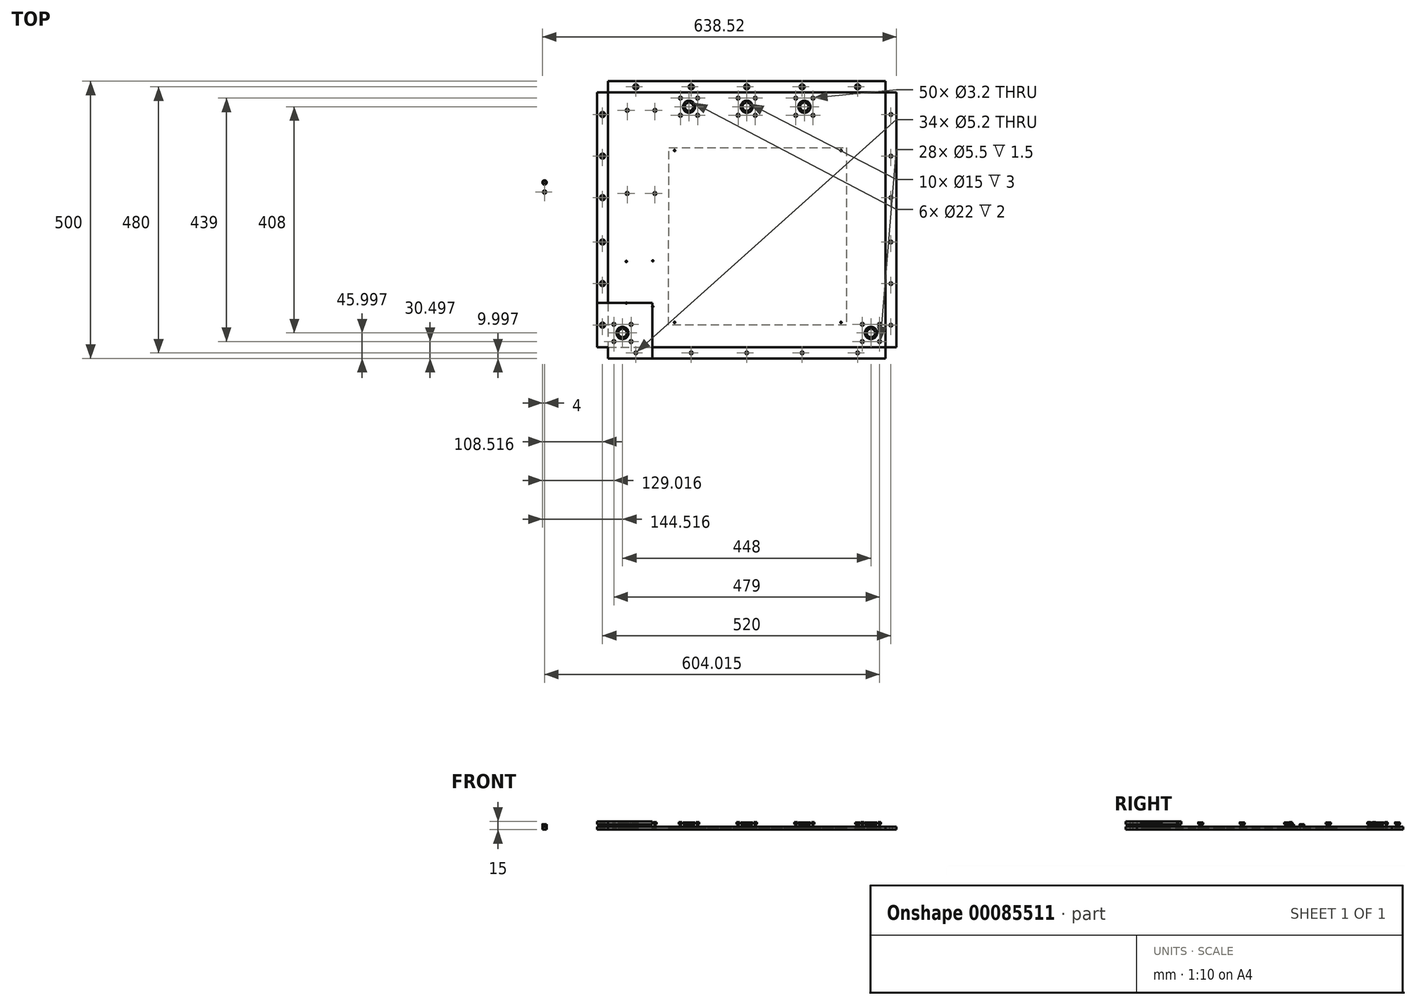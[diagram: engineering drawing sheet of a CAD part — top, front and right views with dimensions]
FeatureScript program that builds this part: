
annotation { "Feature Type Name" : "Feature", "Feature Type Description" : "" }
export const myFeature = defineFeature(function(context is Context, id is Id, definition is map)
    precondition{}
    {
        {
            var Q0;
            Q0=qCreatedBy(makeId("Top.planeOp"),FACE);
            var sketch = newSketch(context, id + "F0", { "sketchPlane" : qUnion([Q0])});
            skLineSegment(sketch, "E0.bottom", {"start": v(-237.36, 309.29) * mm, "end": v(262.64, 309.29) * mm, "construction": true});
            skLineSegment(sketch, "E0.top", {"start": v(-237.36, -150.71) * mm, "end": v(262.64, -150.71) * mm, "construction": true});
            skLineSegment(sketch, "E0.left", {"start": v(-237.36, 309.29) * mm, "end": v(-237.36, -150.71) * mm, "construction": true});
            skLineSegment(sketch, "E0.right", {"start": v(262.64, 309.29) * mm, "end": v(262.64, -150.71) * mm, "construction": true});
            skLineSegment(sketch, "E1.0", {"start": v(-118.36, 309.29) * mm, "end": v(-118.36, -150.71) * mm, "construction": true});
            skLineSegment(sketch, "E2.0", {"start": v(-237.36, 94.29) * mm, "end": v(-117.36, 94.29) * mm, "construction": true});
            skLineSegment(sketch, "E3.0", {"start": v(-202.86, 309.29) * mm, "end": v(-202.86, 94.29) * mm, "construction": true});
            skLineSegment(sketch, "E4.0", {"start": v(-152.86, 309.29) * mm, "end": v(-152.86, 94.29) * mm, "construction": true});
            skLineSegment(sketch, "E5.0", {"start": v(-201.3, 276.79) * mm, "end": v(-118.36, 276.79) * mm, "construction": true});
            skLineSegment(sketch, "E6.0", {"start": v(-201.3, 126.79) * mm, "end": v(-118.36, 126.79) * mm, "construction": true});
            skCircle(sketch, "E7", {"center": v(-202.86, 276.79) * mm, "radius": 1.6 * mm});
            skCircle(sketch, "E8", {"center": v(-152.86, 276.79) * mm, "radius": 1.6 * mm});
            skCircle(sketch, "E9", {"center": v(-152.86, 126.79) * mm, "radius": 1.6 * mm});
            skCircle(sketch, "E10", {"center": v(-202.86, 126.79) * mm, "radius": 1.6 * mm});
            skLineSegment(sketch, "E11.0", {"start": v(182.64, 309.29) * mm, "end": v(182.64, -150.71) * mm, "construction": true});
            skLineSegment(sketch, "E12.0", {"start": v(-117.36, 309.29) * mm, "end": v(-117.36, -150.71) * mm, "construction": true});
            skLineSegment(sketch, "E13.0", {"start": v(197.64, 309.29) * mm, "end": v(197.64, -150.71) * mm, "construction": true});
            skLineSegment(sketch, "E14.0", {"start": v(-132.36, 309.29) * mm, "end": v(-132.36, -150.71) * mm, "construction": true});
            skLineSegment(sketch, "E15.0", {"start": v(-237.36, -140.21) * mm, "end": v(262.64, -140.21) * mm, "construction": true});
            skLineSegment(sketch, "E16.0", {"start": v(-237.36, 298.79) * mm, "end": v(262.64, 298.79) * mm, "construction": true});
            skLineSegment(sketch, "E17.0", {"start": v(-237.36, -109.21) * mm, "end": v(262.64, -109.21) * mm, "construction": true});
            skLineSegment(sketch, "E18.trimOffspring", {"start": v(-226.86, -109.21) * mm, "end": v(-226.86, -140.21) * mm, "construction": true});
            skLineSegment(sketch, "E19.trimOffspring", {"start": v(-195.86, -109.21) * mm, "end": v(-195.86, -140.21) * mm, "construction": true});
            skLineSegment(sketch, "E20", {"start": v(-226.86, -124.71) * mm, "end": v(-195.86, -124.71) * mm, "construction": true});
            skCircle(sketch, "E21", {"center": v(-226.86, -109.21) * mm, "radius": 1.6 * mm});
            skCircle(sketch, "E22", {"center": v(-195.86, -109.21) * mm, "radius": 1.6 * mm});
            skCircle(sketch, "E23", {"center": v(-195.86, -140.21) * mm, "radius": 1.6 * mm});
            skCircle(sketch, "E24", {"center": v(-226.86, -140.21) * mm, "radius": 1.6 * mm});
            skLineSegment(sketch, "E25.trimOffspring", {"start": v(252.14, -109.21) * mm, "end": v(252.14, -140.21) * mm, "construction": true});
            skLineSegment(sketch, "E26.trimOffspring", {"start": v(221.14, -109.21) * mm, "end": v(221.14, -140.21) * mm, "construction": true});
            skLineSegment(sketch, "E27", {"start": v(221.14, -124.71) * mm, "end": v(252.14, -124.71) * mm, "construction": true});
            skCircle(sketch, "E28", {"center": v(221.14, -109.21) * mm, "radius": 1.6 * mm});
            skCircle(sketch, "E29", {"center": v(252.14, -109.21) * mm, "radius": 1.6 * mm});
            skCircle(sketch, "E30", {"center": v(221.14, -140.21) * mm, "radius": 1.6 * mm});
            skCircle(sketch, "E31", {"center": v(252.14, -140.21) * mm, "radius": 1.6 * mm});
            skLineSegment(sketch, "E32.0", {"start": v(-106.86, 309.29) * mm, "end": v(-106.86, 199.29) * mm, "construction": true});
            skLineSegment(sketch, "E33.trimOffspring", {"start": v(197.64, -100.71) * mm, "end": v(262.64, -100.71) * mm, "construction": true});
            skLineSegment(sketch, "E34.trimOffspring", {"start": v(-118.36, 199.29) * mm, "end": v(182.64, 199.29) * mm, "construction": true});
            skLineSegment(sketch, "E35.trimOffspring", {"start": v(-118.36, -100.71) * mm, "end": v(182.64, -100.71) * mm, "construction": true});
            skLineSegment(sketch, "E36.0", {"start": v(132.14, 199.29) * mm, "end": v(132.14, 309.29) * mm, "construction": true});
            skLineSegment(sketch, "E37.0", {"start": v(-75.86, 298.79) * mm, "end": v(-75.86, 267.79) * mm, "construction": true});
            skLineSegment(sketch, "E38.0", {"start": v(101.14, 267.79) * mm, "end": v(101.14, 298.79) * mm, "construction": true});
            skLineSegment(sketch, "E39.0", {"start": v(-237.36, 267.79) * mm, "end": v(262.64, 267.79) * mm, "construction": true});
            skLineSegment(sketch, "E40", {"start": v(101.14, 283.29) * mm, "end": v(132.14, 283.29) * mm, "construction": true});
            skLineSegment(sketch, "E41", {"start": v(-75.86, 283.29) * mm, "end": v(-106.86, 283.29) * mm, "construction": true});
            skCircle(sketch, "E42", {"center": v(101.14, 298.79) * mm, "radius": 1.6 * mm});
            skCircle(sketch, "E43", {"center": v(101.14, 267.79) * mm, "radius": 1.6 * mm});
            skCircle(sketch, "E44", {"center": v(132.14, 298.79) * mm, "radius": 1.6 * mm});
            skCircle(sketch, "E45", {"center": v(132.14, 267.79) * mm, "radius": 1.6 * mm});
            skCircle(sketch, "E46", {"center": v(-75.86, 267.79) * mm, "radius": 1.6 * mm});
            skCircle(sketch, "E47", {"center": v(-75.86, 298.79) * mm, "radius": 1.6 * mm});
            skCircle(sketch, "E48", {"center": v(-106.86, 298.79) * mm, "radius": 1.6 * mm});
            skCircle(sketch, "E49", {"center": v(-106.86, 267.79) * mm, "radius": 1.6 * mm});
            skCircle(sketch, "E50", {"center": v(116.64, 283.29) * mm, "radius": 7.5 * mm});
            skCircle(sketch, "E51", {"center": v(-91.36, 283.29) * mm, "radius": 7.5 * mm});
            skLineSegment(sketch, "E52.0", {"start": v(-237.36, 329.29) * mm, "end": v(262.64, 329.29) * mm});
            skLineSegment(sketch, "E53.0", {"start": v(282.64, 309.29) * mm, "end": v(282.64, -150.71) * mm});
            skLineSegment(sketch, "E54.0", {"start": v(-257.36, 309.29) * mm, "end": v(-257.36, -150.71) * mm});
            skLineSegment(sketch, "E55.0", {"start": v(-237.36, -170.71) * mm, "end": v(262.64, -170.71) * mm});
            skLineSegment(sketch, "E56.0", {"start": v(-237.36, 19.29) * mm, "end": v(-117.36, 19.29) * mm, "construction": true});
            skLineSegment(sketch, "E57.0", {"start": v(-237.36, -84.57) * mm, "end": v(-117.36, -84.57) * mm, "construction": true});
            skLineSegment(sketch, "E58.trimOffspring", {"start": v(-207.36, 19.29) * mm, "end": v(-207.36, -84.57) * mm, "construction": true});
            skLineSegment(sketch, "E59.trimOffspring", {"start": v(-204.36, 19.29) * mm, "end": v(-204.36, -84.57) * mm, "construction": true});
            skLineSegment(sketch, "E60.trimOffspring", {"start": v(-156.66, 19.29) * mm, "end": v(-156.66, -84.57) * mm, "construction": true});
            skLineSegment(sketch, "E61.trimOffspring", {"start": v(-146.14, 19.29) * mm, "end": v(-146.14, -84.57) * mm, "construction": true});
            skLineSegment(sketch, "E62.0", {"start": v(-207.36, 5.39) * mm, "end": v(-146.14, 5.39) * mm, "construction": true});
            skLineSegment(sketch, "E63.0", {"start": v(-207.36, 4.14) * mm, "end": v(-146.14, 4.14) * mm, "construction": true});
            skLineSegment(sketch, "E64.0", {"start": v(-207.36, -70.81) * mm, "end": v(-146.14, -70.81) * mm, "construction": true});
            skLineSegment(sketch, "E65.0", {"start": v(-207.36, -77.16) * mm, "end": v(-146.14, -77.16) * mm, "construction": true});
            skCircle(sketch, "E66", {"center": v(-204.36, 4.14) * mm, "radius": 1.25 * mm});
            skCircle(sketch, "E67", {"center": v(-156.66, 5.39) * mm, "radius": 1.25 * mm});
            skCircle(sketch, "E68", {"center": v(-156.66, -77.16) * mm, "radius": 1.25 * mm});
            skCircle(sketch, "E69", {"center": v(-204.36, -70.81) * mm, "radius": 1.25 * mm});
            skLineSegment(sketch, "E70", {"start": v(262.64, 329.29) * mm, "end": v(262.64, 309.29) * mm});
            skLineSegment(sketch, "E71", {"start": v(262.64, 309.29) * mm, "end": v(282.64, 309.29) * mm});
            skLineSegment(sketch, "E72", {"start": v(-237.36, 329.29) * mm, "end": v(-237.36, 309.29) * mm});
            skLineSegment(sketch, "E73", {"start": v(-257.36, 309.29) * mm, "end": v(-237.36, 309.29) * mm});
            skLineSegment(sketch, "E74", {"start": v(-257.36, -150.71) * mm, "end": v(-237.36, -150.71) * mm});
            skLineSegment(sketch, "E75", {"start": v(-237.36, -170.71) * mm, "end": v(-237.36, -150.71) * mm});
            skLineSegment(sketch, "E76", {"start": v(262.64, -170.71) * mm, "end": v(262.64, -150.71) * mm});
            skLineSegment(sketch, "E77", {"start": v(282.64, -150.71) * mm, "end": v(262.64, -150.71) * mm});
            skLineSegment(sketch, "E78.0", {"start": v(-237.36, 319.29) * mm, "end": v(262.64, 319.29) * mm, "construction": true});
            skLineSegment(sketch, "E79.0", {"start": v(-247.36, 309.29) * mm, "end": v(-247.36, -150.71) * mm, "construction": true});
            skLineSegment(sketch, "E80.0", {"start": v(-257.36, -110.71) * mm, "end": v(-237.36, -110.71) * mm, "construction": true});
            skLineSegment(sketch, "E81.0", {"start": v(-257.36, -35.71) * mm, "end": v(-237.36, -35.71) * mm, "construction": true});
            skLineSegment(sketch, "E82.0", {"start": v(-257.36, 39.29) * mm, "end": v(-237.36, 39.29) * mm, "construction": true});
            skLineSegment(sketch, "E83.0", {"start": v(-257.36, 119.29) * mm, "end": v(-237.36, 119.29) * mm, "construction": true});
            skLineSegment(sketch, "E84.0", {"start": v(-257.36, 194.29) * mm, "end": v(-237.36, 194.29) * mm, "construction": true});
            skLineSegment(sketch, "E85.0", {"start": v(-257.36, 269.29) * mm, "end": v(-237.36, 269.29) * mm, "construction": true});
            skCircle(sketch, "E86", {"center": v(-247.36, 39.29) * mm, "radius": 2.6 * mm});
            skCircle(sketch, "E87", {"center": v(-247.36, 119.29) * mm, "radius": 2.6 * mm});
            skCircle(sketch, "E88", {"center": v(-247.36, 194.29) * mm, "radius": 2.6 * mm});
            skCircle(sketch, "E89", {"center": v(-247.36, 269.29) * mm, "radius": 2.6 * mm});
            skCircle(sketch, "E90", {"center": v(-247.36, -35.71) * mm, "radius": 2.6 * mm});
            skCircle(sketch, "E91", {"center": v(-247.36, -110.71) * mm, "radius": 2.6 * mm});
            skLineSegment(sketch, "E92", {"start": v(12.64, 329.29) * mm, "end": v(12.64, 425.64) * mm});
            skCircle(sketch, "E93.MirrorC", {"center": v(272.64, -110.71) * mm, "radius": 2.6 * mm});
            skCircle(sketch, "E94.MirrorC", {"center": v(272.64, -35.71) * mm, "radius": 2.6 * mm});
            skCircle(sketch, "E95.MirrorC", {"center": v(272.64, 39.29) * mm, "radius": 2.6 * mm});
            skCircle(sketch, "E96.MirrorC", {"center": v(272.64, 119.29) * mm, "radius": 2.6 * mm});
            skCircle(sketch, "E97.MirrorC", {"center": v(272.64, 194.29) * mm, "radius": 2.6 * mm});
            skCircle(sketch, "E98.MirrorC", {"center": v(272.64, 269.29) * mm, "radius": 2.6 * mm});
            skLineSegment(sketch, "E99.0", {"start": v(-187.36, 329.29) * mm, "end": v(-187.36, 309.29) * mm, "construction": true});
            skLineSegment(sketch, "E100.0", {"start": v(-87.36, 329.29) * mm, "end": v(-87.36, 309.29) * mm, "construction": true});
            skLineSegment(sketch, "E101.0", {"start": v(212.64, 329.29) * mm, "end": v(212.64, 309.29) * mm, "construction": true});
            skLineSegment(sketch, "E102.0", {"start": v(112.64, 329.29) * mm, "end": v(112.64, 309.29) * mm, "construction": true});
            skCircle(sketch, "E103", {"center": v(-187.36, 319.29) * mm, "radius": 2.6 * mm});
            skCircle(sketch, "E104", {"center": v(-87.36, 319.29) * mm, "radius": 2.6 * mm});
            skCircle(sketch, "E105", {"center": v(12.64, 319.29) * mm, "radius": 2.6 * mm});
            skCircle(sketch, "E106", {"center": v(112.64, 319.29) * mm, "radius": 2.6 * mm});
            skCircle(sketch, "E107", {"center": v(212.64, 319.29) * mm, "radius": 2.6 * mm});
            skLineSegment(sketch, "E108", {"start": v(282.64, 79.29) * mm, "end": v(335.67, 79.29) * mm});
            skCircle(sketch, "E109.MirrorC", {"center": v(212.64, -160.71) * mm, "radius": 2.6 * mm});
            skCircle(sketch, "E110.MirrorC", {"center": v(112.64, -160.71) * mm, "radius": 2.6 * mm});
            skCircle(sketch, "E111.MirrorC", {"center": v(12.64, -160.71) * mm, "radius": 2.6 * mm});
            skCircle(sketch, "E112.MirrorC", {"center": v(-87.36, -160.71) * mm, "radius": 2.6 * mm});
            skCircle(sketch, "E113.MirrorC", {"center": v(-187.36, -160.71) * mm, "radius": 2.6 * mm});
            skCircle(sketch, "E114", {"center": v(-211.36, -124.71) * mm, "radius": 7.5 * mm});
            skCircle(sketch, "E115", {"center": v(236.64, -124.71) * mm, "radius": 7.5 * mm});
            skLineSegment(sketch, "E116", {"start": v(12.64, 267.79) * mm, "end": v(12.64, 298.79) * mm, "construction": true});
            skLineSegment(sketch, "E117.0", {"start": v(28.14, 267.79) * mm, "end": v(28.14, 298.79) * mm, "construction": true});
            skLineSegment(sketch, "E118.0", {"start": v(-2.86, 267.79) * mm, "end": v(-2.86, 298.79) * mm, "construction": true});
            skCircle(sketch, "E119", {"center": v(12.64, 283.29) * mm, "radius": 7.5 * mm});
            skCircle(sketch, "E120", {"center": v(-2.86, 298.79) * mm, "radius": 1.6 * mm});
            skCircle(sketch, "E121", {"center": v(28.14, 298.79) * mm, "radius": 1.6 * mm});
            skCircle(sketch, "E122", {"center": v(28.14, 267.79) * mm, "radius": 1.6 * mm});
            skCircle(sketch, "E123", {"center": v(-2.86, 267.79) * mm, "radius": 1.6 * mm});
            skSolve(sketch);
        }
        {
            var Q0;
            Q0=qCreatedBy(makeId("Top.planeOp"),FACE);
            var sketch = newSketch(context, id + "F1", { "sketchPlane" : qUnion([Q0])});
            skLineSegment(sketch, "E124.bottom", {"start": v(-558.04, 48.55) * mm, "end": v(-516.04, 48.55) * mm, "construction": true});
            skLineSegment(sketch, "E124.top", {"start": v(-558.04, 1.55) * mm, "end": v(-516.04, 1.55) * mm, "construction": true});
            skLineSegment(sketch, "E124.right", {"start": v(-516.04, 48.55) * mm, "end": v(-516.04, 1.55) * mm, "construction": true});
            skLineSegment(sketch, "E125", {"start": v(-558.04, -28.45) * mm, "end": v(-558.04, 1.55) * mm});
            skLineSegment(sketch, "E126.1", {"start": v(-515.04, 48.55) * mm, "end": v(-515.04, 1.55) * mm, "construction": true});
            skLineSegment(sketch, "E127.0", {"start": v(-473.04, -28.45) * mm, "end": v(-473.04, 1.55) * mm});
            skLineSegment(sketch, "E127.1", {"start": v(-473.04, 48.55) * mm, "end": v(-473.04, 1.55) * mm});
            skLineSegment(sketch, "E128", {"start": v(-515.04, 48.55) * mm, "end": v(-473.04, 48.55) * mm, "construction": true});
            skLineSegment(sketch, "E129", {"start": v(-515.04, 1.55) * mm, "end": v(-473.04, 1.55) * mm, "construction": true});
            skLineSegment(sketch, "E130.bottom", {"start": v(-473.04, -28.45) * mm, "end": v(-558.04, -28.45) * mm});
            skLineSegment(sketch, "E130.top", {"start": v(-473.04, 53.55) * mm, "end": v(-558.04, 53.55) * mm});
            skLineSegment(sketch, "E130.left", {"start": v(-473.04, -28.45) * mm, "end": v(-473.04, 53.55) * mm});
            skLineSegment(sketch, "E131", {"start": v(-558.04, -13.45) * mm, "end": v(-516.04, -13.45) * mm, "construction": true});
            skLineSegment(sketch, "E132.0", {"start": v(-473.04, 75.55) * mm, "end": v(-558.04, 75.55) * mm});
            skLineSegment(sketch, "E133", {"start": v(-558.04, 1.55) * mm, "end": v(-558.04, 53.55) * mm});
            skLineSegment(sketch, "E134", {"start": v(-516.04, 1.55) * mm, "end": v(-516.04, -28.45) * mm, "construction": true});
            skLineSegment(sketch, "E135", {"start": v(-515.04, 1.55) * mm, "end": v(-515.04, -28.45) * mm, "construction": true});
            skLineSegment(sketch, "E136.trimOffspring", {"start": v(-515.04, -13.45) * mm, "end": v(-473.04, -13.45) * mm, "construction": true});
            skCircle(sketch, "E137", {"center": v(-537.04, -13.45) * mm, "radius": 8.5 * mm});
            skCircle(sketch, "E138", {"center": v(-494.04, -13.45) * mm, "radius": 8.5 * mm});
            skSolve(sketch);
        }
        {
            var Q0;
            Q0=makeQuery(id+"F0.imprint","IMPRINT",FACE,{"disambiguationData":[TD([[makeQuery(id+"F0.imprint","IMPRINT",EDGE,{"derivedFrom":sQuery(id+"F0.wireOp",EDGE,"E7")}),-1.0]])]});
            extrude(context, id + "F2", {"entities" : qUnion([Q0]), "depth" : 5 * mm});
        }
        {
            var Q0;
            Q0=makeQuery(id+"F2.opExtrude","CAP_FACE",FACE,{"disambiguationData":[OSD([sQuery(id+"F0.wireOp",EDGE,"E7"),sQuery(id+"F0.wireOp",EDGE,"E8"),sQuery(id+"F0.wireOp",EDGE,"E9"),sQuery(id+"F0.wireOp",EDGE,"E10"),sQuery(id+"F0.wireOp",EDGE,"C0uSwMvh-bZ3V-A5UR-ObhC-SuazAej5d5Y7"),sQuery(id+"F0.wireOp",EDGE,"E21"),sQuery(id+"F0.wireOp",EDGE,"E22"),sQuery(id+"F0.wireOp",EDGE,"E23"),sQuery(id+"F0.wireOp",EDGE,"E24"),sQuery(id+"F0.wireOp",EDGE,"E28"),sQuery(id+"F0.wireOp",EDGE,"E29"),sQuery(id+"F0.wireOp",EDGE,"E30"),sQuery(id+"F0.wireOp",EDGE,"XtzUmerH-F8ZK-TeMd-aJrn-KmrtfTiEuZh9"),sQuery(id+"F0.wireOp",EDGE,"E31"),sQuery(id+"F0.wireOp",EDGE,"ix5QspZB-ting-d7O3-eglK-wTbe0T3LvuQs"),sQuery(id+"F0.wireOp",EDGE,"50q9mh1O-mLyt-XYZc-9GO9-dTGnbKH8VegG"),sQuery(id+"F0.wireOp",EDGE,"E42"),sQuery(id+"F0.wireOp",EDGE,"E43"),sQuery(id+"F0.wireOp",EDGE,"E44"),sQuery(id+"F0.wireOp",EDGE,"E45"),sQuery(id+"F0.wireOp",EDGE,"E46"),sQuery(id+"F0.wireOp",EDGE,"E47"),sQuery(id+"F0.wireOp",EDGE,"E48"),sQuery(id+"F0.wireOp",EDGE,"E49"),sQuery(id+"F0.wireOp",EDGE,"E52.0"),sQuery(id+"F0.wireOp",EDGE,"E53.0"),sQuery(id+"F0.wireOp",EDGE,"E54.0"),sQuery(id+"F0.wireOp",EDGE,"E55.0"),sQuery(id+"F0.wireOp",EDGE,"E66"),sQuery(id+"F0.wireOp",EDGE,"E67"),sQuery(id+"F0.wireOp",EDGE,"E68"),sQuery(id+"F0.wireOp",EDGE,"E69"),sQuery(id+"F0.wireOp",EDGE,"E70"),sQuery(id+"F0.wireOp",EDGE,"E71"),sQuery(id+"F0.wireOp",EDGE,"E72"),sQuery(id+"F0.wireOp",EDGE,"E73"),sQuery(id+"F0.wireOp",EDGE,"E74"),sQuery(id+"F0.wireOp",EDGE,"E75"),sQuery(id+"F0.wireOp",EDGE,"E76"),sQuery(id+"F0.wireOp",EDGE,"E77"),sQuery(id+"F0.wireOp",EDGE,"E86"),sQuery(id+"F0.wireOp",EDGE,"E87"),sQuery(id+"F0.wireOp",EDGE,"E88"),sQuery(id+"F0.wireOp",EDGE,"E89"),sQuery(id+"F0.wireOp",EDGE,"E90"),sQuery(id+"F0.wireOp",EDGE,"E91"),sQuery(id+"F0.wireOp",EDGE,"E93.MirrorC"),sQuery(id+"F0.wireOp",EDGE,"E94.MirrorC"),sQuery(id+"F0.wireOp",EDGE,"E95.MirrorC"),sQuery(id+"F0.wireOp",EDGE,"E96.MirrorC"),sQuery(id+"F0.wireOp",EDGE,"E97.MirrorC"),sQuery(id+"F0.wireOp",EDGE,"E98.MirrorC"),sQuery(id+"F0.wireOp",EDGE,"E103"),sQuery(id+"F0.wireOp",EDGE,"E104"),sQuery(id+"F0.wireOp",EDGE,"E105"),sQuery(id+"F0.wireOp",EDGE,"E106"),sQuery(id+"F0.wireOp",EDGE,"E107"),sQuery(id+"F0.wireOp",EDGE,"E109.MirrorC"),sQuery(id+"F0.wireOp",EDGE,"E110.MirrorC"),sQuery(id+"F0.wireOp",EDGE,"E111.MirrorC"),sQuery(id+"F0.wireOp",EDGE,"E112.MirrorC"),sQuery(id+"F0.wireOp",EDGE,"E113.MirrorC")])],"isStart":false});
            var sketch = newSketch(context, id + "F3", { "sketchPlane" : qUnion([Q0])});
            skCircle(sketch, "E139.0", {"center": v(-202.86, 276.79) * mm, "radius": 1.6 * mm});
            skCircle(sketch, "E139.1", {"center": v(-152.86, 276.79) * mm, "radius": 1.6 * mm});
            skCircle(sketch, "E139.2", {"center": v(-106.86, 267.79) * mm, "radius": 1.6 * mm});
            skCircle(sketch, "E139.3", {"center": v(-106.86, 298.79) * mm, "radius": 1.6 * mm});
            skCircle(sketch, "E139.4", {"center": v(-75.86, 267.79) * mm, "radius": 1.6 * mm});
            skCircle(sketch, "E139.5", {"center": v(-75.86, 298.79) * mm, "radius": 1.6 * mm});
            skCircle(sketch, "E139.7", {"center": v(132.14, 267.79) * mm, "radius": 1.6 * mm});
            skCircle(sketch, "E139.8", {"center": v(132.14, 298.79) * mm, "radius": 1.6 * mm});
            skCircle(sketch, "E139.9", {"center": v(101.14, 298.79) * mm, "radius": 1.6 * mm});
            skCircle(sketch, "E139.10", {"center": v(101.14, 267.79) * mm, "radius": 1.6 * mm});
            skCircle(sketch, "E139.11", {"center": v(-202.86, 126.79) * mm, "radius": 1.6 * mm});
            skCircle(sketch, "E139.12", {"center": v(-152.86, 126.79) * mm, "radius": 1.6 * mm});
            skCircle(sketch, "E139.13", {"center": v(-204.36, 4.14) * mm, "radius": 1.25 * mm});
            skCircle(sketch, "E139.14", {"center": v(-156.66, 5.39) * mm, "radius": 1.25 * mm});
            skCircle(sketch, "E139.15", {"center": v(-156.66, -77.16) * mm, "radius": 1.25 * mm});
            skCircle(sketch, "E139.16", {"center": v(-204.36, -70.81) * mm, "radius": 1.25 * mm});
            skCircle(sketch, "E139.17", {"center": v(-195.86, -109.21) * mm, "radius": 1.6 * mm});
            skCircle(sketch, "E139.18", {"center": v(-226.86, -109.21) * mm, "radius": 1.6 * mm});
            skCircle(sketch, "E139.19", {"center": v(-226.86, -140.21) * mm, "radius": 1.6 * mm});
            skCircle(sketch, "E139.20", {"center": v(-195.86, -140.21) * mm, "radius": 1.6 * mm});
            skCircle(sketch, "E139.23", {"center": v(252.14, -140.21) * mm, "radius": 1.6 * mm});
            skCircle(sketch, "E139.24", {"center": v(252.14, -109.21) * mm, "radius": 1.6 * mm});
            skCircle(sketch, "E139.25", {"center": v(221.14, -109.21) * mm, "radius": 1.6 * mm});
            skCircle(sketch, "E139.26", {"center": v(221.14, -140.21) * mm, "radius": 1.6 * mm});
            skCircle(sketch, "E139.27", {"center": v(272.64, -110.71) * mm, "radius": 2.6 * mm});
            skCircle(sketch, "E139.28", {"center": v(212.64, -160.71) * mm, "radius": 2.6 * mm});
            skCircle(sketch, "E139.29", {"center": v(272.64, -35.71) * mm, "radius": 2.6 * mm});
            skCircle(sketch, "E139.30", {"center": v(112.64, -160.71) * mm, "radius": 2.6 * mm});
            skCircle(sketch, "E139.31", {"center": v(272.64, 39.29) * mm, "radius": 2.6 * mm});
            skCircle(sketch, "E139.32", {"center": v(272.64, 119.29) * mm, "radius": 2.6 * mm});
            skCircle(sketch, "E139.33", {"center": v(272.64, 194.29) * mm, "radius": 2.6 * mm});
            skCircle(sketch, "E139.34", {"center": v(272.64, 269.29) * mm, "radius": 2.6 * mm});
            skCircle(sketch, "E139.35", {"center": v(212.64, 319.29) * mm, "radius": 2.6 * mm});
            skCircle(sketch, "E139.36", {"center": v(112.64, 319.29) * mm, "radius": 2.6 * mm});
            skCircle(sketch, "E139.37", {"center": v(12.64, 319.29) * mm, "radius": 2.6 * mm});
            skCircle(sketch, "E139.38", {"center": v(-87.36, 319.29) * mm, "radius": 2.6 * mm});
            skCircle(sketch, "E139.39", {"center": v(-187.36, 319.29) * mm, "radius": 2.6 * mm});
            skCircle(sketch, "E139.40", {"center": v(-247.36, 269.29) * mm, "radius": 2.6 * mm});
            skCircle(sketch, "E139.41", {"center": v(-247.36, 194.29) * mm, "radius": 2.6 * mm});
            skCircle(sketch, "E139.42", {"center": v(-247.36, 119.29) * mm, "radius": 2.6 * mm});
            skCircle(sketch, "E139.43", {"center": v(-247.36, 39.29) * mm, "radius": 2.6 * mm});
            skCircle(sketch, "E139.44", {"center": v(-247.36, -35.71) * mm, "radius": 2.6 * mm});
            skCircle(sketch, "E139.45", {"center": v(-247.36, -110.71) * mm, "radius": 2.6 * mm});
            skCircle(sketch, "E139.46", {"center": v(-187.36, -160.71) * mm, "radius": 2.6 * mm});
            skCircle(sketch, "E139.47", {"center": v(-87.36, -160.71) * mm, "radius": 2.6 * mm});
            skCircle(sketch, "E139.48", {"center": v(12.64, -160.71) * mm, "radius": 2.6 * mm});
            skCircle(sketch, "E140.0", {"center": v(-91.36, 283.29) * mm, "radius": 7.5 * mm});
            skCircle(sketch, "E140.1", {"center": v(116.64, 283.29) * mm, "radius": 7.5 * mm});
            skCircle(sketch, "E140.2", {"center": v(236.64, -124.71) * mm, "radius": 7.5 * mm});
            skCircle(sketch, "E140.3", {"center": v(-211.36, -124.71) * mm, "radius": 7.5 * mm});
            skCircle(sketch, "E141.0", {"center": v(-211.36, -124.71) * mm, "radius": 11 * mm});
            skCircle(sketch, "E142.0", {"center": v(236.64, -124.71) * mm, "radius": 11 * mm});
            skCircle(sketch, "E143.0", {"center": v(116.64, 283.29) * mm, "radius": 11 * mm});
            skCircle(sketch, "E144.0", {"center": v(-91.36, 283.29) * mm, "radius": 11 * mm});
            skCircle(sketch, "E145.0", {"center": v(-247.36, 269.29) * mm, "radius": 4.6 * mm});
            skCircle(sketch, "E146", {"center": v(-187.36, 319.29) * mm, "radius": 4.6 * mm});
            skCircle(sketch, "E147", {"center": v(-202.86, 276.79) * mm, "radius": 2.75 * mm});
            skCircle(sketch, "E148", {"center": v(-152.86, 276.79) * mm, "radius": 2.75 * mm});
            skCircle(sketch, "E149", {"center": v(-106.86, 267.79) * mm, "radius": 2.75 * mm});
            skCircle(sketch, "E150", {"center": v(-87.36, 319.29) * mm, "radius": 4.6 * mm});
            skCircle(sketch, "E151", {"center": v(12.64, 319.29) * mm, "radius": 4.6 * mm});
            skCircle(sketch, "E152", {"center": v(112.64, 319.29) * mm, "radius": 4.6 * mm});
            skCircle(sketch, "E153", {"center": v(212.64, 319.29) * mm, "radius": 4.6 * mm});
            skCircle(sketch, "E154", {"center": v(272.64, 269.29) * mm, "radius": 4.6 * mm});
            skCircle(sketch, "E155", {"center": v(-106.86, 298.79) * mm, "radius": 2.75 * mm});
            skCircle(sketch, "E156", {"center": v(-75.86, 298.79) * mm, "radius": 2.75 * mm});
            skCircle(sketch, "E157", {"center": v(-75.86, 267.79) * mm, "radius": 2.75 * mm});
            skCircle(sketch, "E158", {"center": v(101.14, 298.79) * mm, "radius": 2.75 * mm});
            skCircle(sketch, "E159", {"center": v(101.14, 267.79) * mm, "radius": 2.75 * mm});
            skCircle(sketch, "E160", {"center": v(132.14, 298.79) * mm, "radius": 2.75 * mm});
            skCircle(sketch, "E161", {"center": v(-247.36, 194.29) * mm, "radius": 4.6 * mm});
            skCircle(sketch, "E162", {"center": v(-247.36, 119.29) * mm, "radius": 4.6 * mm});
            skCircle(sketch, "E163", {"center": v(-202.86, 126.79) * mm, "radius": 2.75 * mm});
            skCircle(sketch, "E164", {"center": v(-152.86, 126.79) * mm, "radius": 2.75 * mm});
            skCircle(sketch, "E165", {"center": v(-247.36, 39.29) * mm, "radius": 4.6 * mm});
            skCircle(sketch, "E166", {"center": v(-247.36, -35.71) * mm, "radius": 4.6 * mm});
            skCircle(sketch, "E167", {"center": v(-247.36, -110.71) * mm, "radius": 4.6 * mm});
            skCircle(sketch, "E168", {"center": v(-187.36, -160.71) * mm, "radius": 4.6 * mm});
            skCircle(sketch, "E169", {"center": v(-87.36, -160.71) * mm, "radius": 4.6 * mm});
            skCircle(sketch, "E170", {"center": v(12.64, -160.71) * mm, "radius": 4.6 * mm});
            skCircle(sketch, "E171", {"center": v(112.64, -160.71) * mm, "radius": 4.6 * mm});
            skCircle(sketch, "E172", {"center": v(-195.86, -109.21) * mm, "radius": 2.75 * mm});
            skCircle(sketch, "E173", {"center": v(-226.86, -109.21) * mm, "radius": 2.75 * mm});
            skCircle(sketch, "E174", {"center": v(-226.86, -140.21) * mm, "radius": 2.75 * mm});
            skCircle(sketch, "E175", {"center": v(-195.86, -140.21) * mm, "radius": 2.75 * mm});
            skCircle(sketch, "E176", {"center": v(272.64, 39.29) * mm, "radius": 4.6 * mm});
            skCircle(sketch, "E177", {"center": v(272.64, -35.71) * mm, "radius": 4.6 * mm});
            skCircle(sketch, "E178", {"center": v(272.64, -110.71) * mm, "radius": 4.6 * mm});
            skCircle(sketch, "E179", {"center": v(221.14, -109.21) * mm, "radius": 2.75 * mm});
            skCircle(sketch, "E180", {"center": v(252.14, -140.21) * mm, "radius": 2.75 * mm});
            skCircle(sketch, "E181", {"center": v(221.14, -140.21) * mm, "radius": 2.75 * mm});
            skCircle(sketch, "E182", {"center": v(252.14, -109.21) * mm, "radius": 2.75 * mm});
            skCircle(sketch, "E183", {"center": v(272.64, 119.29) * mm, "radius": 4.6 * mm});
            skCircle(sketch, "E184", {"center": v(272.64, 194.29) * mm, "radius": 4.6 * mm});
            skCircle(sketch, "E185", {"center": v(132.14, 267.79) * mm, "radius": 2.75 * mm});
            skCircle(sketch, "E186", {"center": v(212.64, -160.71) * mm, "radius": 4.6 * mm});
            skCircle(sketch, "E187.0", {"center": v(12.64, 283.29) * mm, "radius": 7.5 * mm});
            skCircle(sketch, "E187.1", {"center": v(-2.86, 298.79) * mm, "radius": 1.6 * mm});
            skCircle(sketch, "E187.2", {"center": v(28.14, 298.79) * mm, "radius": 1.6 * mm});
            skCircle(sketch, "E187.3", {"center": v(28.14, 267.79) * mm, "radius": 1.6 * mm});
            skCircle(sketch, "E187.4", {"center": v(-2.86, 267.79) * mm, "radius": 1.6 * mm});
            skCircle(sketch, "E188.0", {"center": v(12.64, 283.29) * mm, "radius": 11 * mm});
            skCircle(sketch, "E189", {"center": v(-2.86, 298.79) * mm, "radius": 2.75 * mm});
            skCircle(sketch, "E190", {"center": v(28.14, 298.79) * mm, "radius": 2.75 * mm});
            skCircle(sketch, "E191", {"center": v(28.14, 267.79) * mm, "radius": 2.75 * mm});
            skCircle(sketch, "E192", {"center": v(-2.86, 267.79) * mm, "radius": 2.75 * mm});
            skSolve(sketch);
        }
        {
            var Q0;
            Q0=makeQuery(id+"F3.imprint","IMPRINT",FACE,{"disambiguationData":[TD([[makeQuery(id+"F3.imprint","IMPRINT",EDGE,{"derivedFrom":sQuery(id+"F3.wireOp",EDGE,"E139.3")}),-1.0]])]});
            var Q1;
            Q1=makeQuery(id+"F3.imprint","IMPRINT",FACE,{"disambiguationData":[TD([[makeQuery(id+"F3.imprint","IMPRINT",EDGE,{"derivedFrom":sQuery(id+"F3.wireOp",EDGE,"E139.5")}),-1.0]])]});
            var Q2;
            Q2=makeQuery(id+"F3.imprint","IMPRINT",FACE,{"disambiguationData":[TD([[makeQuery(id+"F3.imprint","IMPRINT",EDGE,{"derivedFrom":sQuery(id+"F3.wireOp",EDGE,"E139.4")}),-1.0]])]});
            var Q3;
            Q3=makeQuery(id+"F3.imprint","IMPRINT",FACE,{"disambiguationData":[TD([[makeQuery(id+"F3.imprint","IMPRINT",EDGE,{"derivedFrom":sQuery(id+"F3.wireOp",EDGE,"E139.2")}),-1.0]])]});
            var Q4;
            Q4=makeQuery(id+"F3.imprint","IMPRINT",FACE,{"disambiguationData":[TD([[makeQuery(id+"F3.imprint","IMPRINT",EDGE,{"derivedFrom":sQuery(id+"F3.wireOp",EDGE,"E139.0")}),-1.0]])]});
            var Q5;
            Q5=makeQuery(id+"F3.imprint","IMPRINT",FACE,{"disambiguationData":[TD([[makeQuery(id+"F3.imprint","IMPRINT",EDGE,{"derivedFrom":sQuery(id+"F3.wireOp",EDGE,"E139.1")}),-1.0]])]});
            var Q6;
            Q6=makeQuery(id+"F3.imprint","IMPRINT",FACE,{"disambiguationData":[TD([[makeQuery(id+"F3.imprint","IMPRINT",EDGE,{"derivedFrom":sQuery(id+"F3.wireOp",EDGE,"E139.11")}),-1.0]])]});
            var Q7;
            Q7=makeQuery(id+"F3.imprint","IMPRINT",FACE,{"disambiguationData":[TD([[makeQuery(id+"F3.imprint","IMPRINT",EDGE,{"derivedFrom":sQuery(id+"F3.wireOp",EDGE,"E139.12")}),-1.0]])]});
            var Q8;
            Q8=makeQuery(id+"F3.imprint","IMPRINT",FACE,{"disambiguationData":[TD([[makeQuery(id+"F3.imprint","IMPRINT",EDGE,{"derivedFrom":sQuery(id+"F3.wireOp",EDGE,"E139.18")}),-1.0]])]});
            var Q9;
            Q9=makeQuery(id+"F3.imprint","IMPRINT",FACE,{"disambiguationData":[TD([[makeQuery(id+"F3.imprint","IMPRINT",EDGE,{"derivedFrom":sQuery(id+"F3.wireOp",EDGE,"E139.17")}),-1.0]])]});
            var Q10;
            Q10=makeQuery(id+"F3.imprint","IMPRINT",FACE,{"disambiguationData":[TD([[makeQuery(id+"F3.imprint","IMPRINT",EDGE,{"derivedFrom":sQuery(id+"F3.wireOp",EDGE,"E139.20")}),-1.0]])]});
            var Q11;
            Q11=makeQuery(id+"F3.imprint","IMPRINT",FACE,{"disambiguationData":[TD([[makeQuery(id+"F3.imprint","IMPRINT",EDGE,{"derivedFrom":sQuery(id+"F3.wireOp",EDGE,"E139.19")}),-1.0]])]});
            var Q12;
            Q12=makeQuery(id+"F3.imprint","IMPRINT",FACE,{"disambiguationData":[TD([[makeQuery(id+"F3.imprint","IMPRINT",EDGE,{"derivedFrom":sQuery(id+"F3.wireOp",EDGE,"E139.24")}),-1.0]])]});
            var Q13;
            Q13=makeQuery(id+"F3.imprint","IMPRINT",FACE,{"disambiguationData":[TD([[makeQuery(id+"F3.imprint","IMPRINT",EDGE,{"derivedFrom":sQuery(id+"F3.wireOp",EDGE,"E139.25")}),-1.0]])]});
            var Q14;
            Q14=makeQuery(id+"F3.imprint","IMPRINT",FACE,{"disambiguationData":[TD([[makeQuery(id+"F3.imprint","IMPRINT",EDGE,{"derivedFrom":sQuery(id+"F3.wireOp",EDGE,"E139.26")}),-1.0]])]});
            var Q15;
            Q15=makeQuery(id+"F3.imprint","IMPRINT",FACE,{"disambiguationData":[TD([[makeQuery(id+"F3.imprint","IMPRINT",EDGE,{"derivedFrom":sQuery(id+"F3.wireOp",EDGE,"E139.23")}),-1.0]])]});
            var Q16;
            Q16=makeQuery(id+"F3.imprint","IMPRINT",FACE,{"disambiguationData":[TD([[makeQuery(id+"F3.imprint","IMPRINT",EDGE,{"derivedFrom":sQuery(id+"F3.wireOp",EDGE,"E139.9")}),-1.0]])]});
            var Q17;
            Q17=makeQuery(id+"F3.imprint","IMPRINT",FACE,{"disambiguationData":[TD([[makeQuery(id+"F3.imprint","IMPRINT",EDGE,{"derivedFrom":sQuery(id+"F3.wireOp",EDGE,"E139.10")}),-1.0]])]});
            var Q18;
            Q18=makeQuery(id+"F3.imprint","IMPRINT",FACE,{"disambiguationData":[TD([[makeQuery(id+"F3.imprint","IMPRINT",EDGE,{"derivedFrom":sQuery(id+"F3.wireOp",EDGE,"E139.8")}),-1.0]])]});
            var Q19;
            Q19=makeQuery(id+"F3.imprint","IMPRINT",FACE,{"disambiguationData":[TD([[makeQuery(id+"F3.imprint","IMPRINT",EDGE,{"derivedFrom":sQuery(id+"F3.wireOp",EDGE,"E139.7")}),-1.0]])]});
            var Q20;
            Q20=makeQuery(id+"F3.imprint","IMPRINT",FACE,{"disambiguationData":[TD([[makeQuery(id+"F3.imprint","IMPRINT",EDGE,{"derivedFrom":sQuery(id+"F3.wireOp",EDGE,"E187.1")}),-1.0]])]});
            var Q21;
            Q21=makeQuery(id+"F3.imprint","IMPRINT",FACE,{"disambiguationData":[TD([[makeQuery(id+"F3.imprint","IMPRINT",EDGE,{"derivedFrom":sQuery(id+"F3.wireOp",EDGE,"E187.2")}),-1.0]])]});
            var Q22;
            Q22=makeQuery(id+"F3.imprint","IMPRINT",FACE,{"disambiguationData":[TD([[makeQuery(id+"F3.imprint","IMPRINT",EDGE,{"derivedFrom":sQuery(id+"F3.wireOp",EDGE,"E187.3")}),-1.0]])]});
            var Q23;
            Q23=makeQuery(id+"F3.imprint","IMPRINT",FACE,{"disambiguationData":[TD([[makeQuery(id+"F3.imprint","IMPRINT",EDGE,{"derivedFrom":sQuery(id+"F3.wireOp",EDGE,"E187.4")}),-1.0]])]});
            extrude(context, id + "F4", {"entities" : qUnion([Q0, Q1, Q2, Q3, Q4, Q5, Q6, Q7, Q8, Q9, Q10, Q11, Q12, Q13, Q14, Q15, Q16, Q17, Q18, Q19, Q20, Q21, Q22, Q23]), "operationType" : NewBodyOperationType.REMOVE, "oppositeDirection" : true, "depth" : 1.5 * mm});
        }
        {
            var Q0;
            Q0=makeQuery(id+"F3.imprint","IMPRINT",FACE,{"disambiguationData":[TD([[makeQuery(id+"F3.imprint","IMPRINT",EDGE,{"derivedFrom":sQuery(id+"F3.wireOp",EDGE,"E140.1")}),-1.0]])]});
            var Q1;
            Q1=makeQuery(id+"F3.imprint","IMPRINT",FACE,{"disambiguationData":[TD([[makeQuery(id+"F3.imprint","IMPRINT",EDGE,{"derivedFrom":sQuery(id+"F3.wireOp",EDGE,"E139.36")}),-1.0]])]});
            var Q2;
            Q2=makeQuery(id+"F3.imprint","IMPRINT",FACE,{"disambiguationData":[TD([[makeQuery(id+"F3.imprint","IMPRINT",EDGE,{"derivedFrom":sQuery(id+"F3.wireOp",EDGE,"E139.37")}),-1.0]])]});
            var Q3;
            Q3=makeQuery(id+"F3.imprint","IMPRINT",FACE,{"disambiguationData":[TD([[makeQuery(id+"F3.imprint","IMPRINT",EDGE,{"derivedFrom":sQuery(id+"F3.wireOp",EDGE,"E139.38")}),-1.0]])]});
            var Q4;
            Q4=makeQuery(id+"F3.imprint","IMPRINT",FACE,{"disambiguationData":[TD([[makeQuery(id+"F3.imprint","IMPRINT",EDGE,{"derivedFrom":sQuery(id+"F3.wireOp",EDGE,"E139.39")}),-1.0]])]});
            var Q5;
            Q5=makeQuery(id+"F3.imprint","IMPRINT",FACE,{"disambiguationData":[TD([[makeQuery(id+"F3.imprint","IMPRINT",EDGE,{"derivedFrom":sQuery(id+"F3.wireOp",EDGE,"E139.40")}),-1.0]])]});
            var Q6;
            Q6=makeQuery(id+"F3.imprint","IMPRINT",FACE,{"disambiguationData":[TD([[makeQuery(id+"F3.imprint","IMPRINT",EDGE,{"derivedFrom":sQuery(id+"F3.wireOp",EDGE,"E139.41")}),-1.0]])]});
            var Q7;
            Q7=makeQuery(id+"F3.imprint","IMPRINT",FACE,{"disambiguationData":[TD([[makeQuery(id+"F3.imprint","IMPRINT",EDGE,{"derivedFrom":sQuery(id+"F3.wireOp",EDGE,"E139.42")}),-1.0]])]});
            var Q8;
            Q8=makeQuery(id+"F3.imprint","IMPRINT",FACE,{"disambiguationData":[TD([[makeQuery(id+"F3.imprint","IMPRINT",EDGE,{"derivedFrom":sQuery(id+"F3.wireOp",EDGE,"E139.43")}),-1.0]])]});
            var Q9;
            Q9=makeQuery(id+"F3.imprint","IMPRINT",FACE,{"disambiguationData":[TD([[makeQuery(id+"F3.imprint","IMPRINT",EDGE,{"derivedFrom":sQuery(id+"F3.wireOp",EDGE,"E139.44")}),-1.0]])]});
            var Q10;
            Q10=makeQuery(id+"F3.imprint","IMPRINT",FACE,{"disambiguationData":[TD([[makeQuery(id+"F3.imprint","IMPRINT",EDGE,{"derivedFrom":sQuery(id+"F3.wireOp",EDGE,"E139.45")}),-1.0]])]});
            var Q11;
            Q11=makeQuery(id+"F3.imprint","IMPRINT",FACE,{"disambiguationData":[TD([[makeQuery(id+"F3.imprint","IMPRINT",EDGE,{"derivedFrom":sQuery(id+"F3.wireOp",EDGE,"E139.46")}),1.0]])]});
            var Q12;
            Q12=makeQuery(id+"F3.imprint","IMPRINT",FACE,{"disambiguationData":[TD([[makeQuery(id+"F3.imprint","IMPRINT",EDGE,{"derivedFrom":sQuery(id+"F3.wireOp",EDGE,"E139.47")}),1.0]])]});
            var Q13;
            Q13=makeQuery(id+"F3.imprint","IMPRINT",FACE,{"disambiguationData":[TD([[makeQuery(id+"F3.imprint","IMPRINT",EDGE,{"derivedFrom":sQuery(id+"F3.wireOp",EDGE,"E139.48")}),1.0]])]});
            var Q14;
            Q14=makeQuery(id+"F3.imprint","IMPRINT",FACE,{"disambiguationData":[TD([[makeQuery(id+"F3.imprint","IMPRINT",EDGE,{"derivedFrom":sQuery(id+"F3.wireOp",EDGE,"E139.30")}),1.0]])]});
            var Q15;
            Q15=makeQuery(id+"F3.imprint","IMPRINT",FACE,{"disambiguationData":[TD([[makeQuery(id+"F3.imprint","IMPRINT",EDGE,{"derivedFrom":sQuery(id+"F3.wireOp",EDGE,"E139.27")}),1.0]])]});
            var Q16;
            Q16=makeQuery(id+"F3.imprint","IMPRINT",FACE,{"disambiguationData":[TD([[makeQuery(id+"F3.imprint","IMPRINT",EDGE,{"derivedFrom":sQuery(id+"F3.wireOp",EDGE,"E140.2")}),-1.0]])]});
            var Q17;
            Q17=makeQuery(id+"F3.imprint","IMPRINT",FACE,{"disambiguationData":[TD([[makeQuery(id+"F3.imprint","IMPRINT",EDGE,{"derivedFrom":sQuery(id+"F3.wireOp",EDGE,"E140.3")}),-1.0]])]});
            var Q18;
            Q18=makeQuery(id+"F3.imprint","IMPRINT",FACE,{"disambiguationData":[TD([[makeQuery(id+"F3.imprint","IMPRINT",EDGE,{"derivedFrom":sQuery(id+"F3.wireOp",EDGE,"E139.29")}),1.0]])]});
            var Q19;
            Q19=makeQuery(id+"F3.imprint","IMPRINT",FACE,{"disambiguationData":[TD([[makeQuery(id+"F3.imprint","IMPRINT",EDGE,{"derivedFrom":sQuery(id+"F3.wireOp",EDGE,"E139.31")}),1.0]])]});
            var Q20;
            Q20=makeQuery(id+"F3.imprint","IMPRINT",FACE,{"disambiguationData":[TD([[makeQuery(id+"F3.imprint","IMPRINT",EDGE,{"derivedFrom":sQuery(id+"F3.wireOp",EDGE,"E139.32")}),1.0]])]});
            var Q21;
            Q21=makeQuery(id+"F3.imprint","IMPRINT",FACE,{"disambiguationData":[TD([[makeQuery(id+"F3.imprint","IMPRINT",EDGE,{"derivedFrom":sQuery(id+"F3.wireOp",EDGE,"E139.34")}),1.0]])]});
            var Q22;
            Q22=makeQuery(id+"F3.imprint","IMPRINT",FACE,{"disambiguationData":[TD([[makeQuery(id+"F3.imprint","IMPRINT",EDGE,{"derivedFrom":sQuery(id+"F3.wireOp",EDGE,"E139.33")}),1.0]])]});
            var Q23;
            Q23=makeQuery(id+"F3.imprint","IMPRINT",FACE,{"disambiguationData":[TD([[makeQuery(id+"F3.imprint","IMPRINT",EDGE,{"derivedFrom":sQuery(id+"F3.wireOp",EDGE,"E139.35")}),-1.0]])]});
            var Q24;
            Q24=makeQuery(id+"F3.imprint","IMPRINT",FACE,{"disambiguationData":[TD([[makeQuery(id+"F3.imprint","IMPRINT",EDGE,{"derivedFrom":sQuery(id+"F3.wireOp",EDGE,"E140.0")}),-1.0]])]});
            var Q25;
            Q25=makeQuery(id+"F3.imprint","IMPRINT",FACE,{"disambiguationData":[TD([[makeQuery(id+"F3.imprint","IMPRINT",EDGE,{"derivedFrom":sQuery(id+"F3.wireOp",EDGE,"E139.28")}),1.0]])]});
            var Q26;
            Q26=makeQuery(id+"F3.imprint","IMPRINT",FACE,{"disambiguationData":[TD([[makeQuery(id+"F3.imprint","IMPRINT",EDGE,{"derivedFrom":sQuery(id+"F3.wireOp",EDGE,"E187.0")}),-1.0]])]});
            extrude(context, id + "F5", {"entities" : qUnion([Q0, Q1, Q2, Q3, Q4, Q5, Q6, Q7, Q8, Q9, Q10, Q11, Q12, Q13, Q14, Q15, Q16, Q17, Q18, Q19, Q20, Q21, Q22, Q23, Q24, Q25, Q26]), "operationType" : NewBodyOperationType.REMOVE, "oppositeDirection" : true, "depth" : 2 * mm});
        }
        {
            var Q0;
            Q0=qCreatedBy(makeId("Top.planeOp"),FACE);
            var sketch = newSketch(context, id + "F6", { "sketchPlane" : qUnion([Q0])});
            skCircle(sketch, "E193", {"center": v(-351.88, 146.77) * mm, "radius": 2.6 * mm});
            skCircle(sketch, "E194", {"center": v(-351.88, 146.77) * mm, "radius": 4 * mm});
            skCircle(sketch, "E195", {"center": v(-351.88, 129.43) * mm, "radius": 3 * mm});
            skCircle(sketch, "E196", {"center": v(-351.88, 129.43) * mm, "radius": 1.6 * mm});
            skCircle(sketch, "E197", {"center": v(-328.87, 125.57) * mm, "radius": 4.06 * mm});
            skCircle(sketch, "E198", {"center": v(-328.87, 125.57) * mm, "radius": 6.44 * mm});
            skCircle(sketch, "E199", {"center": v(-328.87, 125.57) * mm, "radius": 9.26 * mm});
            skCircle(sketch, "E200", {"center": v(-325, 147.79) * mm, "radius": 4.8 * mm});
            skSolve(sketch);
        }
        {
            var Q0;
            Q0=makeQuery(id+"F6.imprint","IMPRINT",FACE,{"disambiguationData":[TD([[makeQuery(id+"F6.imprint","IMPRINT",EDGE,{"derivedFrom":sQuery(id+"F6.wireOp",EDGE,"E195")}),1.0]])]});
            var Q1;
            Q1=makeQuery(id+"F6.imprint","IMPRINT",FACE,{"disambiguationData":[TD([[makeQuery(id+"F6.imprint","IMPRINT",EDGE,{"derivedFrom":sQuery(id+"F6.wireOp",EDGE,"E193")}),-1.0]])]});
            extrude(context, id + "F7", {"entities" : qUnion([Q0, Q1]), "depth" : 5 * mm});
        }
        {
            var Q0;
            Q0=makeQuery(id+"F6.imprint","IMPRINT",FACE,{"disambiguationData":[TD([[makeQuery(id+"F6.imprint","IMPRINT",EDGE,{"derivedFrom":sQuery(id+"F6.wireOp",EDGE,"E193")}),-1.0]])]});
            var Q1;
            Q1=makeQuery(id+"F6.imprint","IMPRINT",FACE,{"disambiguationData":[TD([[makeQuery(id+"F6.imprint","IMPRINT",EDGE,{"derivedFrom":sQuery(id+"F6.wireOp",EDGE,"E195")}),1.0]])]});
            extrude(context, id + "F8", {"entities" : qUnion([Q0, Q1]), "depth" : 10 * mm});
        }
        {
            var Q0;
            Q0=makeQuery(id+"F0.imprint","IMPRINT",FACE,{"disambiguationData":[TD([[makeQuery(id+"F0.imprint","IMPRINT",EDGE,{"derivedFrom":sQuery(id+"F0.wireOp",EDGE,"E7")}),-1.0]])]});
            var sketch = newSketch(context, id + "F9", { "sketchPlane" : qUnion([Q0])});
            skLineSegment(sketch, "E201.0", {"start": v(-237.36, 309.29) * mm, "end": v(-237.36, -150.71) * mm});
            skLineSegment(sketch, "E201.1", {"start": v(-237.36, 309.29) * mm, "end": v(262.64, 309.29) * mm});
            skLineSegment(sketch, "E201.2", {"start": v(262.64, 309.29) * mm, "end": v(262.64, -150.71) * mm});
            skLineSegment(sketch, "E201.3", {"start": v(-237.36, -150.71) * mm, "end": v(262.64, -150.71) * mm});
            skCircle(sketch, "E201.4", {"center": v(-211.36, -124.71) * mm, "radius": 7.5 * mm});
            skCircle(sketch, "E201.5", {"center": v(236.64, -124.71) * mm, "radius": 7.5 * mm});
            skCircle(sketch, "E201.6", {"center": v(12.64, 283.29) * mm, "radius": 7.5 * mm});
            skCircle(sketch, "E201.7", {"center": v(116.64, 283.29) * mm, "radius": 7.5 * mm});
            skCircle(sketch, "E201.8", {"center": v(-91.36, 283.29) * mm, "radius": 7.5 * mm});
            skLineSegment(sketch, "E201.9", {"start": v(-118.36, 199.29) * mm, "end": v(182.64, 199.29) * mm});
            skLineSegment(sketch, "E201.10", {"start": v(182.64, 199.29) * mm, "end": v(182.64, -100.71) * mm});
            skLineSegment(sketch, "E201.12", {"start": v(-118.36, -100.71) * mm, "end": v(182.64, -100.71) * mm});
            skLineSegment(sketch, "E202.0", {"start": v(-117.36, 199.29) * mm, "end": v(-117.36, -100.71) * mm});
            skPoint(sketch, "E203.orphan", {"position": v(-117.36, -150.71) * mm});
            skPoint(sketch, "E204.orphan", {"position": v(182.64, -150.71) * mm});
            skPoint(sketch, "E205.orphan", {"position": v(182.64, 309.29) * mm});
            skPoint(sketch, "E206.orphan", {"position": v(-117.36, 309.29) * mm});
            skLineSegment(sketch, "E207.0", {"start": v(-558.04, -28.45) * mm, "end": v(-558.04, 1.55) * mm});
            skLineSegment(sketch, "E207.1", {"start": v(-558.04, 1.55) * mm, "end": v(-558.04, 53.55) * mm});
            skLineSegment(sketch, "E207.2", {"start": v(-473.04, 53.55) * mm, "end": v(-558.04, 53.55) * mm});
            skLineSegment(sketch, "E207.3", {"start": v(-473.04, -28.45) * mm, "end": v(-473.04, 53.55) * mm});
            skLineSegment(sketch, "E207.4", {"start": v(-473.04, -28.45) * mm, "end": v(-558.04, -28.45) * mm});
            skCircle(sketch, "E207.5", {"center": v(-494.04, -13.45) * mm, "radius": 8.5 * mm});
            skCircle(sketch, "E207.6", {"center": v(-537.04, -13.45) * mm, "radius": 8.5 * mm});
            skLineSegment(sketch, "E207.7", {"start": v(-473.04, 75.55) * mm, "end": v(-558.04, 75.55) * mm});
            skLineSegment(sketch, "E208.bottom", {"start": v(-568.04, 85.55) * mm, "end": v(-463.04, 85.55) * mm});
            skLineSegment(sketch, "E208.top", {"start": v(-568.04, -38.45) * mm, "end": v(-463.04, -38.45) * mm});
            skLineSegment(sketch, "E208.left", {"start": v(-568.04, 85.55) * mm, "end": v(-568.04, -38.45) * mm});
            skLineSegment(sketch, "E208.right", {"start": v(-463.04, 85.55) * mm, "end": v(-463.04, -38.45) * mm});
            skLineSegment(sketch, "E209.bottom", {"start": v(-127.36, 209.29) * mm, "end": v(192.64, 209.29) * mm});
            skLineSegment(sketch, "E209.top", {"start": v(-117.36, -110.71) * mm, "end": v(192.64, -110.71) * mm});
            skLineSegment(sketch, "E209.left", {"start": v(-127.36, 199.29) * mm, "end": v(-127.36, 102.57) * mm});
            skLineSegment(sketch, "E209.right", {"start": v(192.64, 199.29) * mm, "end": v(192.64, 137.6) * mm});
            skLineSegment(sketch, "E210", {"start": v(32.64, -110.71) * mm, "end": v(32.64, -100.71) * mm, "construction": true});
            skLineSegment(sketch, "E211", {"start": v(32.64, 209.29) * mm, "end": v(32.64, 199.29) * mm, "construction": true});
            skLineSegment(sketch, "E212.0", {"start": v(-117.36, 209.29) * mm, "end": v(-117.36, 199.29) * mm, "construction": true});
            skLineSegment(sketch, "E213.0", {"start": v(182.64, 209.29) * mm, "end": v(182.64, 199.29) * mm, "construction": true});
            skLineSegment(sketch, "E214.0", {"start": v(-117.36, -110.71) * mm, "end": v(-117.36, -100.71) * mm, "construction": true});
            skLineSegment(sketch, "E215.0", {"start": v(182.64, -110.71) * mm, "end": v(182.64, -100.71) * mm, "construction": true});
            skCircle(sketch, "E216", {"center": v(-117.36, 204.29) * mm, "radius": 1.25 * mm});
            skCircle(sketch, "E217", {"center": v(182.64, 204.29) * mm, "radius": 1.25 * mm});
            skCircle(sketch, "E218", {"center": v(182.64, -105.71) * mm, "radius": 1.25 * mm});
            skCircle(sketch, "E219", {"center": v(-117.36, -105.71) * mm, "radius": 1.25 * mm});
            skLineSegment(sketch, "E220.0", {"start": v(-237.36, -135.71) * mm, "end": v(-222.36, -135.71) * mm});
            skLineSegment(sketch, "E221.0", {"start": v(247.64, 294.29) * mm, "end": v(247.64, 209.29) * mm});
            skLineSegment(sketch, "E222.0", {"start": v(-222.36, 294.29) * mm, "end": v(-111, 294.29) * mm});
            skArc(sketch, "E223.0", {"start": v(-111, 294.29) * mm, "mid": v(-91.36, 260.79) * mm, "end": v(-71.74, 294.29) * mm});
            skArc(sketch, "E224.0", {"start": v(-7, 294.29) * mm, "mid": v(12.64, 260.79) * mm, "end": v(32.26, 294.29) * mm});
            skArc(sketch, "E225.0", {"start": v(97, 294.29) * mm, "mid": v(116.64, 260.79) * mm, "end": v(136.26, 294.29) * mm});
            skArc(sketch, "E226.0", {"start": v(-231, -135.71) * mm, "mid": v(-227.27, -140.62) * mm, "end": v(-222.36, -144.34) * mm});
            skArc(sketch, "E227.0", {"start": v(247.64, -144.34) * mm, "mid": v(252.55, -140.62) * mm, "end": v(256.26, -135.71) * mm});
            skLineSegment(sketch, "E228.trimOffspring", {"start": v(-222.36, -135.71) * mm, "end": v(-222.36, -150.71) * mm});
            skArc(sketch, "E229.trimOffspring", {"start": v(-191.74, -135.71) * mm, "mid": v(-195.45, -108.8) * mm, "end": v(-222.36, -105.09) * mm});
            skLineSegment(sketch, "E230.trimOffspring", {"start": v(-191.74, -135.71) * mm, "end": v(-141.5, -135.71) * mm});
            skLineSegment(sketch, "E231.trimOffspring", {"start": v(247.64, -135.71) * mm, "end": v(262.64, -135.71) * mm});
            skLineSegment(sketch, "E232.trimOffspring", {"start": v(247.64, -135.71) * mm, "end": v(247.64, -150.71) * mm});
            skArc(sketch, "E233.trimOffspring", {"start": v(247.64, -105.09) * mm, "mid": v(220.73, -108.8) * mm, "end": v(217, -135.71) * mm});
            skLineSegment(sketch, "E234.trimOffspring", {"start": v(136.26, 294.29) * mm, "end": v(247.64, 294.29) * mm});
            skLineSegment(sketch, "E235.trimOffspring", {"start": v(32.26, 294.29) * mm, "end": v(97, 294.29) * mm});
            skLineSegment(sketch, "E236.trimOffspring", {"start": v(-71.74, 294.29) * mm, "end": v(-7, 294.29) * mm});
            skLineSegment(sketch, "E237", {"start": v(192.64, 209.29) * mm, "end": v(247.64, 209.29) * mm});
            skLineSegment(sketch, "E238.0", {"start": v(206.03, 199.29) * mm, "end": v(247.64, 199.29) * mm});
            skLineSegment(sketch, "E239.0", {"start": v(-118.36, 189.29) * mm, "end": v(-117.36, 189.29) * mm});
            skLineSegment(sketch, "E240.0", {"start": v(172.64, 189.29) * mm, "end": v(172.64, -90.71) * mm});
            skLineSegment(sketch, "E241.0", {"start": v(-107.36, 189.29) * mm, "end": v(-107.36, -90.71) * mm});
            skLineSegment(sketch, "E242.0", {"start": v(-118.36, -90.71) * mm, "end": v(-117.36, -90.71) * mm});
            skLineSegment(sketch, "E243.trimOffspring", {"start": v(-107.36, -90.71) * mm, "end": v(172.64, -90.71) * mm});
            skLineSegment(sketch, "E244.trimOffspring", {"start": v(-107.36, 189.29) * mm, "end": v(172.64, 189.29) * mm});
            skLineSegment(sketch, "E245.0", {"start": v(-42.36, 189.29) * mm, "end": v(-42.36, -90.71) * mm});
            skLineSegment(sketch, "E246.0", {"start": v(-32.36, 189.29) * mm, "end": v(-32.36, -90.71) * mm});
            skLineSegment(sketch, "E247.0", {"start": v(27.64, 189.29) * mm, "end": v(27.64, -90.71) * mm});
            skLineSegment(sketch, "E248.0", {"start": v(37.64, 189.29) * mm, "end": v(37.64, -90.71) * mm});
            skLineSegment(sketch, "E249.0", {"start": v(97.64, 189.29) * mm, "end": v(97.64, -90.71) * mm});
            skLineSegment(sketch, "E250.0", {"start": v(107.64, 189.29) * mm, "end": v(107.64, -90.71) * mm});
            skLineSegment(sketch, "E251", {"start": v(-127.36, 209.29) * mm, "end": v(-222.36, 209.29) * mm});
            skLineSegment(sketch, "E252.0", {"start": v(-127.36, 199.29) * mm, "end": v(-222.36, 199.29) * mm});
            skLineSegment(sketch, "E253", {"start": v(-127.36, -110.71) * mm, "end": v(-127.36, -135.71) * mm});
            skLineSegment(sketch, "E254", {"start": v(192.64, -110.71) * mm, "end": v(192.64, -135.71) * mm});
            skLineSegment(sketch, "E255", {"start": v(192.64, -135.71) * mm, "end": v(247.64, -70.17) * mm});
            skLineSegment(sketch, "E256", {"start": v(-127.36, -135.71) * mm, "end": v(-222.36, -40.71) * mm});
            skLineSegment(sketch, "E257", {"start": v(192.64, -120.16) * mm, "end": v(247.64, -54.6) * mm});
            skLineSegment(sketch, "E258", {"start": v(247.64, -54.6) * mm, "end": v(192.64, -54.6) * mm});
            skLineSegment(sketch, "E259.0", {"start": v(247.64, -44.6) * mm, "end": v(192.64, -44.6) * mm});
            skLineSegment(sketch, "E260", {"start": v(247.64, -44.6) * mm, "end": v(192.64, 20.94) * mm});
            skLineSegment(sketch, "E261", {"start": v(247.64, -29.05) * mm, "end": v(192.64, 36.5) * mm});
            skLineSegment(sketch, "E262", {"start": v(192.64, 36.5) * mm, "end": v(247.64, 36.5) * mm});
            skLineSegment(sketch, "E263.0", {"start": v(192.64, 46.5) * mm, "end": v(247.64, 46.5) * mm});
            skLineSegment(sketch, "E264", {"start": v(192.64, 46.5) * mm, "end": v(247.64, 112.04) * mm});
            skLineSegment(sketch, "E265", {"start": v(192.64, 62.05) * mm, "end": v(247.64, 127.6) * mm});
            skLineSegment(sketch, "E266", {"start": v(247.64, 127.6) * mm, "end": v(192.64, 127.6) * mm});
            skLineSegment(sketch, "E267.0", {"start": v(247.64, 137.6) * mm, "end": v(192.64, 137.6) * mm});
            skLineSegment(sketch, "E268", {"start": v(247.64, 137.6) * mm, "end": v(192.64, 199.29) * mm});
            skLineSegment(sketch, "E269", {"start": v(206.03, 199.29) * mm, "end": v(247.64, 152.62) * mm});
            skLineSegment(sketch, "E270.trimOffspring", {"start": v(247.64, 112.04) * mm, "end": v(247.64, 46.5) * mm});
            skLineSegment(sketch, "E271.trimOffspring", {"start": v(247.64, 199.29) * mm, "end": v(247.64, 152.62) * mm});
            skLineSegment(sketch, "E272.trimOffspring", {"start": v(192.64, 127.6) * mm, "end": v(192.64, 62.05) * mm});
            skLineSegment(sketch, "E273.trimOffspring", {"start": v(192.64, 20.94) * mm, "end": v(192.64, -110.71) * mm});
            skLineSegment(sketch, "E274.trimOffspring", {"start": v(247.64, 36.5) * mm, "end": v(247.64, -29.05) * mm});
            skLineSegment(sketch, "E275.trimOffspring", {"start": v(247.64, -70.17) * mm, "end": v(247.64, -105.09) * mm});
            skLineSegment(sketch, "E276", {"start": v(-141.5, -135.71) * mm, "end": v(-222.36, -54.86) * mm});
            skLineSegment(sketch, "E277", {"start": v(-222.36, -40.71) * mm, "end": v(-127.36, -40.71) * mm});
            skLineSegment(sketch, "E278.0", {"start": v(-222.36, -30.71) * mm, "end": v(-127.36, -30.71) * mm});
            skLineSegment(sketch, "E279", {"start": v(-222.36, -30.71) * mm, "end": v(-127.36, 64.29) * mm});
            skLineSegment(sketch, "E280", {"start": v(-222.36, -16.57) * mm, "end": v(-127.36, 78.43) * mm});
            skLineSegment(sketch, "E281", {"start": v(-127.36, 78.43) * mm, "end": v(-222.36, 78.43) * mm});
            skLineSegment(sketch, "E282", {"start": v(-222.36, 88.43) * mm, "end": v(-127.36, 88.43) * mm});
            skLineSegment(sketch, "E283", {"start": v(-127.36, 88.43) * mm, "end": v(-222.36, 183.43) * mm});
            skLineSegment(sketch, "E284", {"start": v(-127.36, 102.57) * mm, "end": v(-222.36, 197.57) * mm});
            skLineSegment(sketch, "E285.trimOffspring", {"start": v(-127.36, -135.71) * mm, "end": v(217, -135.71) * mm});
            skLineSegment(sketch, "E286.trimOffspring", {"start": v(-127.36, -40.71) * mm, "end": v(-127.36, -110.71) * mm});
            skLineSegment(sketch, "E287.trimOffspring", {"start": v(-127.36, 64.29) * mm, "end": v(-127.36, -30.71) * mm});
            skLineSegment(sketch, "E288.trimOffspring", {"start": v(-222.36, -54.86) * mm, "end": v(-222.36, -105.09) * mm});
            skLineSegment(sketch, "E289.trimOffspring", {"start": v(-222.36, 78.43) * mm, "end": v(-222.36, -16.57) * mm});
            skLineSegment(sketch, "E290.trimOffspring", {"start": v(-222.36, 199.29) * mm, "end": v(-222.36, 197.57) * mm});
            skLineSegment(sketch, "E291", {"start": v(-222.36, 294.29) * mm, "end": v(-222.36, 209.29) * mm});
            skLineSegment(sketch, "E292.trimOffspring", {"start": v(-222.36, 183.43) * mm, "end": v(-222.36, 88.43) * mm});
            skLineSegment(sketch, "E293", {"start": v(-222.36, 209.29) * mm, "end": v(-137.36, 294.29) * mm});
            skLineSegment(sketch, "E294", {"start": v(-222.36, 223.43) * mm, "end": v(-151.5, 294.29) * mm});
            skLineSegment(sketch, "E295", {"start": v(-127.36, 209.29) * mm, "end": v(-127.36, 294.29) * mm});
            skLineSegment(sketch, "E296.0", {"start": v(-117.36, 209.29) * mm, "end": v(-117.36, 294.29) * mm});
            skLineSegment(sketch, "E297", {"start": v(-117.36, 294.29) * mm, "end": v(-32.36, 209.29) * mm});
            skLineSegment(sketch, "E298", {"start": v(-18.22, 209.29) * mm, "end": v(-75.89, 266.95) * mm});
            skLineSegment(sketch, "E299", {"start": v(-18.22, 209.29) * mm, "end": v(-18.22, 294.29) * mm});
            skLineSegment(sketch, "E300.0", {"start": v(-8.22, 209.29) * mm, "end": v(-8.22, 294.29) * mm});
            skLineSegment(sketch, "E301", {"start": v(-8.22, 209.29) * mm, "end": v(76.78, 294.29) * mm});
            skLineSegment(sketch, "E302", {"start": v(5.92, 209.29) * mm, "end": v(90.92, 294.29) * mm});
            skLineSegment(sketch, "E303", {"start": v(90.92, 294.29) * mm, "end": v(90.92, 209.29) * mm});
            skLineSegment(sketch, "E304.0", {"start": v(100.92, 294.29) * mm, "end": v(100.92, 209.29) * mm});
            skLineSegment(sketch, "E305", {"start": v(100.92, 294.29) * mm, "end": v(185.92, 209.29) * mm});
            skLineSegment(sketch, "E306", {"start": v(200.06, 209.29) * mm, "end": v(115.06, 294.29) * mm});
            skLineSegment(sketch, "E307", {"start": v(200.06, 209.29) * mm, "end": v(200.06, 294.29) * mm});
            skLineSegment(sketch, "E308.0", {"start": v(210.06, 209.29) * mm, "end": v(210.06, 294.29) * mm});
            skSolve(sketch);
        }
        {
            var Q0;
            {var subQ0=sQuery(id+"F9.wireOp",EDGE,"E241.0");Q0=makeQuery(id+"F9.imprint","IMPRINT",FACE,{"disambiguationData":[TD([[makeQuery(id+"F9.imprint","IMPRINT",EDGE,{"derivedFrom":subQ0}),1.0]])]});}
            var sketch = newSketch(context, id + "F10", { "sketchPlane" : qUnion([Q0])});
            skLineSegment(sketch, "E309.0", {"start": v(-237.36, 309.29) * mm, "end": v(262.64, 309.29) * mm});
            skLineSegment(sketch, "E309.1", {"start": v(-237.36, 309.29) * mm, "end": v(-237.36, -150.71) * mm});
            skLineSegment(sketch, "E309.2", {"start": v(-237.36, -150.71) * mm, "end": v(262.64, -150.71) * mm});
            skLineSegment(sketch, "E309.3", {"start": v(262.64, 309.29) * mm, "end": v(262.64, -150.71) * mm});
            skCircle(sketch, "E309.4", {"center": v(12.64, 283.29) * mm, "radius": 7.5 * mm});
            skCircle(sketch, "E309.5", {"center": v(236.64, -124.71) * mm, "radius": 7.5 * mm});
            skCircle(sketch, "E309.6", {"center": v(-211.36, -124.71) * mm, "radius": 7.5 * mm});
            skCircle(sketch, "E309.7", {"center": v(-117.36, 204.29) * mm, "radius": 1.25 * mm});
            skCircle(sketch, "E309.8", {"center": v(-117.36, -105.71) * mm, "radius": 1.25 * mm});
            skCircle(sketch, "E309.9", {"center": v(182.64, -105.71) * mm, "radius": 1.25 * mm});
            skCircle(sketch, "E309.10", {"center": v(182.64, 204.29) * mm, "radius": 1.25 * mm});
            skLineSegment(sketch, "E309.11", {"start": v(-127.36, 209.29) * mm, "end": v(192.64, 209.29) * mm});
            skLineSegment(sketch, "E309.12", {"start": v(-117.36, -110.71) * mm, "end": v(192.64, -110.71) * mm});
            skLineSegment(sketch, "E310", {"start": v(-117.36, -110.71) * mm, "end": v(-128.56, -110.71) * mm});
            skLineSegment(sketch, "E311", {"start": v(-128.56, -110.71) * mm, "end": v(-127.36, 209.29) * mm});
            skLineSegment(sketch, "E312", {"start": v(192.64, 209.29) * mm, "end": v(192.64, -110.71) * mm});
            skSolve(sketch);
        }
        {
            var Q0;
            Q0=makeQuery(id+"F10.imprint","IMPRINT",FACE,{"disambiguationData":[TD([[makeQuery(id+"F10.imprint","IMPRINT",EDGE,{"derivedFrom":sQuery(id+"F10.wireOp",EDGE,"E309.0")}),-1.0]])]});
            var Q1;
            Q1=makeQuery(id+"F10.imprint","IMPRINT",FACE,{"disambiguationData":[TD([[makeQuery(id+"F10.imprint","IMPRINT",EDGE,{"derivedFrom":sQuery(id+"F10.wireOp",EDGE,"E309.7")}),-1.0]])]});
            var Q2;
            {var subQ0=sQuery(id+"F9.wireOp",EDGE,"E241.0");Q2=makeQuery(id+"F10.imprint","IMPRINT",FACE,{"disambiguationData":[TD([[makeQuery(id+"F10.imprint","IMPRINT",EDGE,{"derivedFrom":makeQuery(id+"F9.imprint","IMPRINT",EDGE,{"derivedFrom":subQ0})}),1.0]])]});}
            extrude(context, id + "F11", {"entities" : qUnion([Q0, Q1, Q2]), "depth" : 5 * mm});
        }
        {
            var Q0;
            Q0=makeQuery(id+"F10.imprint","IMPRINT",FACE,{"disambiguationData":[TD([[makeQuery(id+"F10.imprint","IMPRINT",EDGE,{"derivedFrom":sQuery(id+"F10.wireOp",EDGE,"E309.7")}),-1.0]])]});
            var Q1;
            {var subQ0=sQuery(id+"F9.wireOp",EDGE,"E241.0");Q1=makeQuery(id+"F10.imprint","IMPRINT",FACE,{"disambiguationData":[TD([[makeQuery(id+"F10.imprint","IMPRINT",EDGE,{"derivedFrom":makeQuery(id+"F9.imprint","IMPRINT",EDGE,{"derivedFrom":subQ0})}),1.0]])]});}
            extrude(context, id + "F12", {"entities" : qUnion([Q0, Q1]), "depth" : 3 * mm});
        }
        {
            var Q0;
            Q0=makeQuery(id+"F2.opExtrude","SWEPT_BODY",BODY,{"disambiguationData":[OSD([sQuery(id+"F0.wireOp",EDGE,"E7"),sQuery(id+"F0.wireOp",EDGE,"E8"),sQuery(id+"F0.wireOp",EDGE,"E9"),sQuery(id+"F0.wireOp",EDGE,"E10"),sQuery(id+"F0.wireOp",EDGE,"E21"),sQuery(id+"F0.wireOp",EDGE,"E22"),sQuery(id+"F0.wireOp",EDGE,"E23"),sQuery(id+"F0.wireOp",EDGE,"E24"),sQuery(id+"F0.wireOp",EDGE,"E28"),sQuery(id+"F0.wireOp",EDGE,"E29"),sQuery(id+"F0.wireOp",EDGE,"E30"),sQuery(id+"F0.wireOp",EDGE,"E31"),sQuery(id+"F0.wireOp",EDGE,"E42"),sQuery(id+"F0.wireOp",EDGE,"E43"),sQuery(id+"F0.wireOp",EDGE,"E44"),sQuery(id+"F0.wireOp",EDGE,"E45"),sQuery(id+"F0.wireOp",EDGE,"E46"),sQuery(id+"F0.wireOp",EDGE,"E47"),sQuery(id+"F0.wireOp",EDGE,"E48"),sQuery(id+"F0.wireOp",EDGE,"E49"),sQuery(id+"F0.wireOp",EDGE,"E50"),sQuery(id+"F0.wireOp",EDGE,"E51"),sQuery(id+"F0.wireOp",EDGE,"E52.0"),sQuery(id+"F0.wireOp",EDGE,"E53.0"),sQuery(id+"F0.wireOp",EDGE,"E54.0"),sQuery(id+"F0.wireOp",EDGE,"E55.0"),sQuery(id+"F0.wireOp",EDGE,"E66"),sQuery(id+"F0.wireOp",EDGE,"E67"),sQuery(id+"F0.wireOp",EDGE,"E68"),sQuery(id+"F0.wireOp",EDGE,"E69"),sQuery(id+"F0.wireOp",EDGE,"E70"),sQuery(id+"F0.wireOp",EDGE,"E71"),sQuery(id+"F0.wireOp",EDGE,"E72"),sQuery(id+"F0.wireOp",EDGE,"E73"),sQuery(id+"F0.wireOp",EDGE,"E74"),sQuery(id+"F0.wireOp",EDGE,"E75"),sQuery(id+"F0.wireOp",EDGE,"E76"),sQuery(id+"F0.wireOp",EDGE,"E77"),sQuery(id+"F0.wireOp",EDGE,"E86"),sQuery(id+"F0.wireOp",EDGE,"E87"),sQuery(id+"F0.wireOp",EDGE,"E88"),sQuery(id+"F0.wireOp",EDGE,"E89"),sQuery(id+"F0.wireOp",EDGE,"E90"),sQuery(id+"F0.wireOp",EDGE,"E91"),sQuery(id+"F0.wireOp",EDGE,"E93.MirrorC"),sQuery(id+"F0.wireOp",EDGE,"E94.MirrorC"),sQuery(id+"F0.wireOp",EDGE,"E95.MirrorC"),sQuery(id+"F0.wireOp",EDGE,"E96.MirrorC"),sQuery(id+"F0.wireOp",EDGE,"E97.MirrorC"),sQuery(id+"F0.wireOp",EDGE,"E98.MirrorC"),sQuery(id+"F0.wireOp",EDGE,"E103"),sQuery(id+"F0.wireOp",EDGE,"E104"),sQuery(id+"F0.wireOp",EDGE,"E105"),sQuery(id+"F0.wireOp",EDGE,"E106"),sQuery(id+"F0.wireOp",EDGE,"E107"),sQuery(id+"F0.wireOp",EDGE,"E109.MirrorC"),sQuery(id+"F0.wireOp",EDGE,"E110.MirrorC"),sQuery(id+"F0.wireOp",EDGE,"E111.MirrorC"),sQuery(id+"F0.wireOp",EDGE,"E112.MirrorC"),sQuery(id+"F0.wireOp",EDGE,"E113.MirrorC"),sQuery(id+"F0.wireOp",EDGE,"E114"),sQuery(id+"F0.wireOp",EDGE,"E115"),sQuery(id+"F0.wireOp",EDGE,"E119"),sQuery(id+"F0.wireOp",EDGE,"E120"),sQuery(id+"F0.wireOp",EDGE,"E121"),sQuery(id+"F0.wireOp",EDGE,"E122"),sQuery(id+"F0.wireOp",EDGE,"E123")])]});
            transform(context, id + "F13", {"entities" : qUnion([Q0]), "transformType" : TransformType.TRANSLATION_3D, "dx" : 0 * mm, "dy" : 0 * mm, "dz" : 10 * mm, "makeCopy" : true});
        }
        {
            var Q0;
            Q0=makeQuery(id+"F13.opPattern","COPY",FACE,{"derivedFrom":makeQuery(id+"F2.opExtrude","CAP_FACE",FACE,{"disambiguationData":[OSD([sQuery(id+"F0.wireOp",EDGE,"E7"),sQuery(id+"F0.wireOp",EDGE,"E8"),sQuery(id+"F0.wireOp",EDGE,"E9"),sQuery(id+"F0.wireOp",EDGE,"E10"),sQuery(id+"F0.wireOp",EDGE,"E21"),sQuery(id+"F0.wireOp",EDGE,"E22"),sQuery(id+"F0.wireOp",EDGE,"E23"),sQuery(id+"F0.wireOp",EDGE,"E24"),sQuery(id+"F0.wireOp",EDGE,"E28"),sQuery(id+"F0.wireOp",EDGE,"E29"),sQuery(id+"F0.wireOp",EDGE,"E30"),sQuery(id+"F0.wireOp",EDGE,"E31"),sQuery(id+"F0.wireOp",EDGE,"E42"),sQuery(id+"F0.wireOp",EDGE,"E43"),sQuery(id+"F0.wireOp",EDGE,"E44"),sQuery(id+"F0.wireOp",EDGE,"E45"),sQuery(id+"F0.wireOp",EDGE,"E46"),sQuery(id+"F0.wireOp",EDGE,"E47"),sQuery(id+"F0.wireOp",EDGE,"E48"),sQuery(id+"F0.wireOp",EDGE,"E49"),sQuery(id+"F0.wireOp",EDGE,"E50"),sQuery(id+"F0.wireOp",EDGE,"E51"),sQuery(id+"F0.wireOp",EDGE,"E52.0"),sQuery(id+"F0.wireOp",EDGE,"E53.0"),sQuery(id+"F0.wireOp",EDGE,"E54.0"),sQuery(id+"F0.wireOp",EDGE,"E55.0"),sQuery(id+"F0.wireOp",EDGE,"E66"),sQuery(id+"F0.wireOp",EDGE,"E67"),sQuery(id+"F0.wireOp",EDGE,"E68"),sQuery(id+"F0.wireOp",EDGE,"E69"),sQuery(id+"F0.wireOp",EDGE,"E70"),sQuery(id+"F0.wireOp",EDGE,"E71"),sQuery(id+"F0.wireOp",EDGE,"E72"),sQuery(id+"F0.wireOp",EDGE,"E73"),sQuery(id+"F0.wireOp",EDGE,"E74"),sQuery(id+"F0.wireOp",EDGE,"E75"),sQuery(id+"F0.wireOp",EDGE,"E76"),sQuery(id+"F0.wireOp",EDGE,"E77"),sQuery(id+"F0.wireOp",EDGE,"E86"),sQuery(id+"F0.wireOp",EDGE,"E87"),sQuery(id+"F0.wireOp",EDGE,"E88"),sQuery(id+"F0.wireOp",EDGE,"E89"),sQuery(id+"F0.wireOp",EDGE,"E90"),sQuery(id+"F0.wireOp",EDGE,"E91"),sQuery(id+"F0.wireOp",EDGE,"E93.MirrorC"),sQuery(id+"F0.wireOp",EDGE,"E94.MirrorC"),sQuery(id+"F0.wireOp",EDGE,"E95.MirrorC"),sQuery(id+"F0.wireOp",EDGE,"E96.MirrorC"),sQuery(id+"F0.wireOp",EDGE,"E97.MirrorC"),sQuery(id+"F0.wireOp",EDGE,"E98.MirrorC"),sQuery(id+"F0.wireOp",EDGE,"E103"),sQuery(id+"F0.wireOp",EDGE,"E104"),sQuery(id+"F0.wireOp",EDGE,"E105"),sQuery(id+"F0.wireOp",EDGE,"E106"),sQuery(id+"F0.wireOp",EDGE,"E107"),sQuery(id+"F0.wireOp",EDGE,"E109.MirrorC"),sQuery(id+"F0.wireOp",EDGE,"E110.MirrorC"),sQuery(id+"F0.wireOp",EDGE,"E111.MirrorC"),sQuery(id+"F0.wireOp",EDGE,"E112.MirrorC"),sQuery(id+"F0.wireOp",EDGE,"E113.MirrorC"),sQuery(id+"F0.wireOp",EDGE,"E114"),sQuery(id+"F0.wireOp",EDGE,"E115"),sQuery(id+"F0.wireOp",EDGE,"E119"),sQuery(id+"F0.wireOp",EDGE,"E120"),sQuery(id+"F0.wireOp",EDGE,"E121"),sQuery(id+"F0.wireOp",EDGE,"E122"),sQuery(id+"F0.wireOp",EDGE,"E123")])],"isStart":false}),"instanceName":"1"});
            var sketch = newSketch(context, id + "F14", { "sketchPlane" : qUnion([Q0])});
            skLineSegment(sketch, "E313.0", {"start": v(-157.36, 309.29) * mm, "end": v(-157.36, -150.71) * mm});
            skLineSegment(sketch, "E314.0", {"start": v(-237.36, -70.71) * mm, "end": v(262.64, -70.71) * mm});
            skLineSegment(sketch, "E315", {"start": v(-237.36, -70.71) * mm, "end": v(-257.36, -70.71) * mm});
            skLineSegment(sketch, "E316", {"start": v(-157.36, -150.71) * mm, "end": v(-157.36, -170.71) * mm});
            skLineSegment(sketch, "E317.0", {"start": v(-237.36, -175.71) * mm, "end": v(262.64, -175.71) * mm});
            skLineSegment(sketch, "E318.0", {"start": v(-262.36, 309.29) * mm, "end": v(-262.36, -150.71) * mm});
            skSolve(sketch);
        }
        {
            var Q0;
            {var subQ7=sQuery(id+"F14.wireOp",EDGE,"E315");Q0=makeQuery(id+"F14.imprint","IMPRINT",FACE,{"disambiguationData":[TD([[makeQuery(id+"F14.imprint","IMPRINT",EDGE,{"derivedFrom":subQ7}),-1.0]])]});}
            extrude(context, id + "F15", {"entities" : qUnion([Q0]), "operationType" : NewBodyOperationType.REMOVE, "oppositeDirection" : true, "depth" : 5 * mm});
        }
    });
